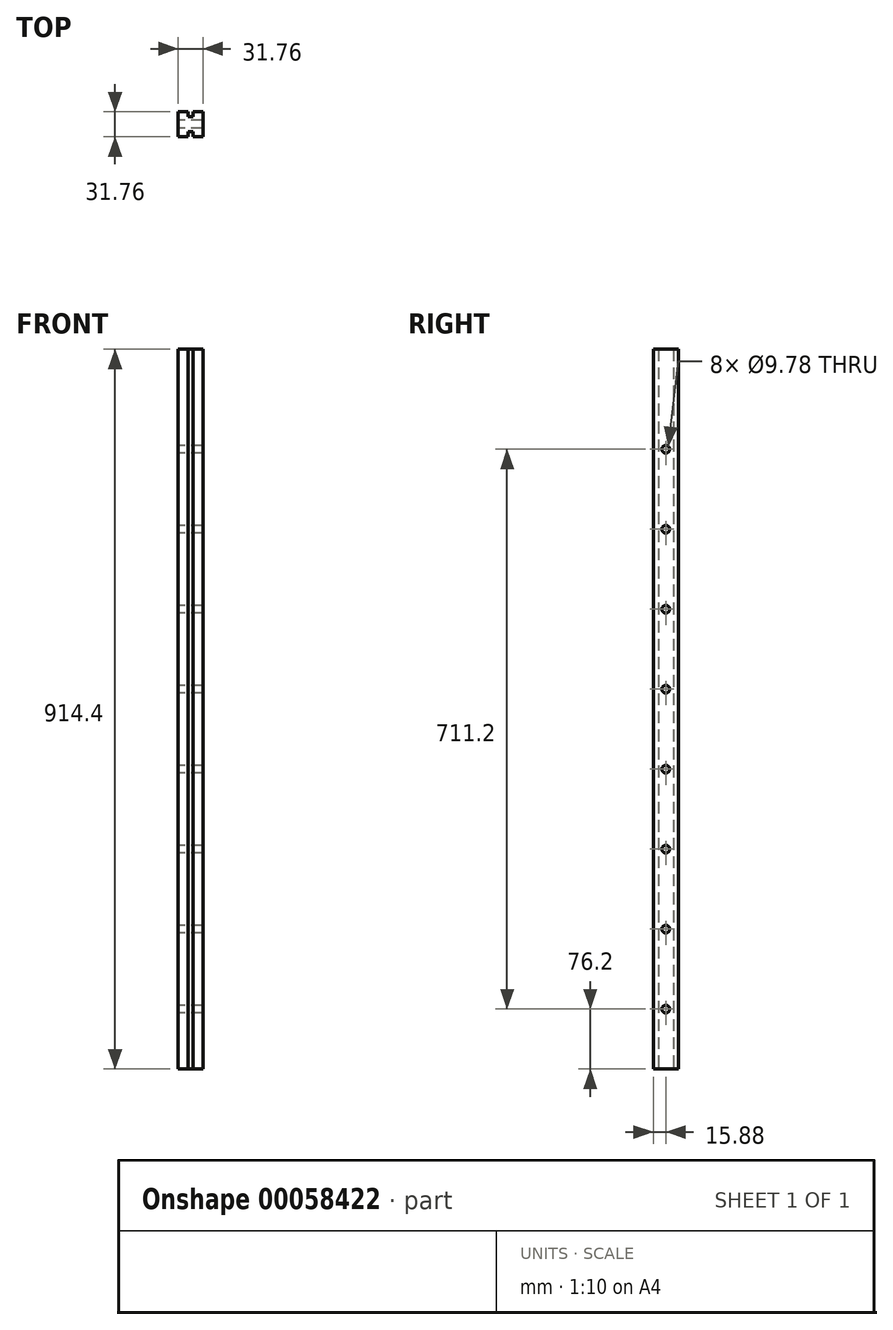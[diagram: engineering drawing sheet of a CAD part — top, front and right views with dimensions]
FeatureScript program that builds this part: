
annotation { "Feature Type Name" : "Feature", "Feature Type Description" : "" }
export const myFeature = defineFeature(function(context is Context, id is Id, definition is map)
    precondition{}
    {
        {
            var Q0;
            Q0=qCreatedBy(makeId("Top.planeOp"),FACE);
            var sketch = newSketch(context, id + "F0", { "sketchPlane" : qUnion([Q0])});
            skLineSegment(sketch, "E0.rect.bottom", {"start": v(15.88, -15.87) * mm, "end": v(3.18, -15.88) * mm});
            skLineSegment(sketch, "E0.rect.top", {"start": v(15.87, 15.88) * mm, "end": v(3.17, 15.87) * mm});
            skLineSegment(sketch, "E0.rect.left", {"start": v(15.88, -15.87) * mm, "end": v(15.87, 15.88) * mm});
            skLineSegment(sketch, "E0.rect.right", {"start": v(-15.87, -15.88) * mm, "end": v(-15.88, 15.87) * mm});
            skPoint(sketch, "E0.rect.middle", {"position": v(0, 0) * mm});
            skLineSegment(sketch, "E1", {"start": v(-3.18, 15.87) * mm, "end": v(-3.18, 9.52) * mm});
            skLineSegment(sketch, "E2", {"start": v(-3.18, 9.52) * mm, "end": v(3.17, 9.52) * mm});
            skLineSegment(sketch, "E3", {"start": v(3.17, 9.52) * mm, "end": v(3.17, 15.87) * mm});
            skLineSegment(sketch, "E4", {"start": v(-3.17, -15.88) * mm, "end": v(-3.17, -9.53) * mm});
            skLineSegment(sketch, "E5", {"start": v(-3.17, -9.53) * mm, "end": v(3.18, -9.52) * mm});
            skLineSegment(sketch, "E6", {"start": v(3.18, -9.53) * mm, "end": v(3.18, -15.88) * mm});
            skLineSegment(sketch, "E7", {"start": v(0, 9.52) * mm, "end": v(0, -9.53) * mm, "construction": true});
            skLineSegment(sketch, "E8.trimOffspring", {"start": v(-3.18, 15.87) * mm, "end": v(-15.88, 15.87) * mm});
            skLineSegment(sketch, "E9.trimOffspring", {"start": v(-3.17, -15.88) * mm, "end": v(-15.87, -15.88) * mm});
            skSolve(sketch);
        }
        {
            var Q0;
            Q0 = qSketchRegion(id + "F0", true);
            extrude(context, id + "F1", {"entities" : qUnion([Q0]), "depth" : 914.4 * mm});
        }
        {
            var Q0;
            Q0=makeQuery(id+"F1.opExtrude","SWEPT_FACE",FACE,{"disambiguationData":[OSD([sQuery(id+"F0.wireOp",EDGE,"E0.rect.right")])]});
            var sketch = newSketch(context, id + "F2", { "sketchPlane" : qUnion([Q0])});
            skLineSegment(sketch, "E10", {"start": v(0, 0) * mm, "end": v(0, 914.4) * mm, "construction": true});
            skCircle(sketch, "E11", {"center": v(0, 787.4) * mm, "radius": 4.89 * mm});
            skCircle(sketch, "E12", {"center": v(0, 685.8) * mm, "radius": 4.89 * mm});
            skCircle(sketch, "E13", {"center": v(0, 584.2) * mm, "radius": 4.89 * mm});
            skCircle(sketch, "E14", {"center": v(0, 482.6) * mm, "radius": 4.89 * mm});
            skCircle(sketch, "E15", {"center": v(0, 381) * mm, "radius": 4.89 * mm});
            skCircle(sketch, "E16", {"center": v(0, 279.4) * mm, "radius": 4.89 * mm});
            skCircle(sketch, "E17", {"center": v(0, 177.8) * mm, "radius": 4.89 * mm});
            skCircle(sketch, "E18", {"center": v(0, 76.2) * mm, "radius": 4.89 * mm});
            skSolve(sketch);
        }
        {
            var Q0;
            Q0 = qSketchRegion(id + "F2", true);
            extrude(context, id + "F3", {"entities" : qUnion([Q0]), "operationType" : NewBodyOperationType.REMOVE, "endBound" : BoundingType.THROUGH_ALL, "oppositeDirection" : true, "depth" : 25.4 * mm});
        }
    });
